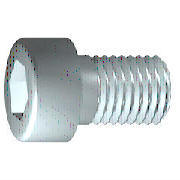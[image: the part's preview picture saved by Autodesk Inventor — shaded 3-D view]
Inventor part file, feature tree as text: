
AUTODESK INVENTOR PART (.ipt)
format: ipt  version: 2019 (Build 230136000, 136)  size: 196,608 bytes
history: native  units: mm (DEFAULTED — no unit token found)
features: sketch x2, extrude x1, plane x1, fillet x1
ambient origin geometry x7: Origin, YZ Plane, XY Plane, X Axis, Y Axis, Z Axis, Center Point
bodies: Solid1 (feature_tree), Body (feature_tree)
feature tree (5):
  extrude  "Slot"  Depth=6.0mm
  plane  "Work Plane1"
  fillet  "Fillet2"  Radius=6.0mm
  sketch  "Sketch1"  dims[d1=17.5mm d2=0.61355mm d3=6.0mm]
  sketch  "Sketch2"  dims[d4=3.0mm d5=60.0deg d6=6.0mm d7=6.0mm d8=5.773503mm d9=10.0mm d10=90.0deg d11=10.0mm d12=0.0mm d13=17.5mm d14=0.0mm d15=0.61345mm d16=0.61345mm d17=0.6mm d19=0.0mm d26=20.0mm d27=45.0deg d28=0.0mm d29=0.0mm d30=0.1mm]
